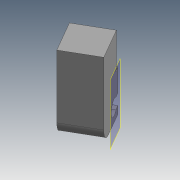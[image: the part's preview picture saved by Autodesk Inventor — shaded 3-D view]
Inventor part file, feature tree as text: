
AUTODESK INVENTOR PART (.ipt)
format: ipt  version: 2014 SP1 (Build 180222100, 222)  size: 103,936 bytes
history: native  units: in
note: dims shown in document units (in); Inventor stores cm internally (conversion verified against a paired STEP export)
features: plane x1, extrude x1, sketch x1
ambient origin geometry x8: Origin, YZ Plane, XZ Plane, XY Plane, X Axis, Y Axis, Z Axis, Center Point
bodies: Solid1 (feature_tree)
feature tree (3):
  plane  "Work Plane1"
  extrude  "Extrusion1"  Depth=0.3409in TaperAngle=0.0deg
  sketch  "Sketch1"  dims[d2=0.125in d3=0.3409in d4=0.0in d9=0.3409in d10=0.75in d12=0.6201in d13=0.0738in d14=0.0541in d15=0.0541in d16=0.0295in d17=0.0394in]
